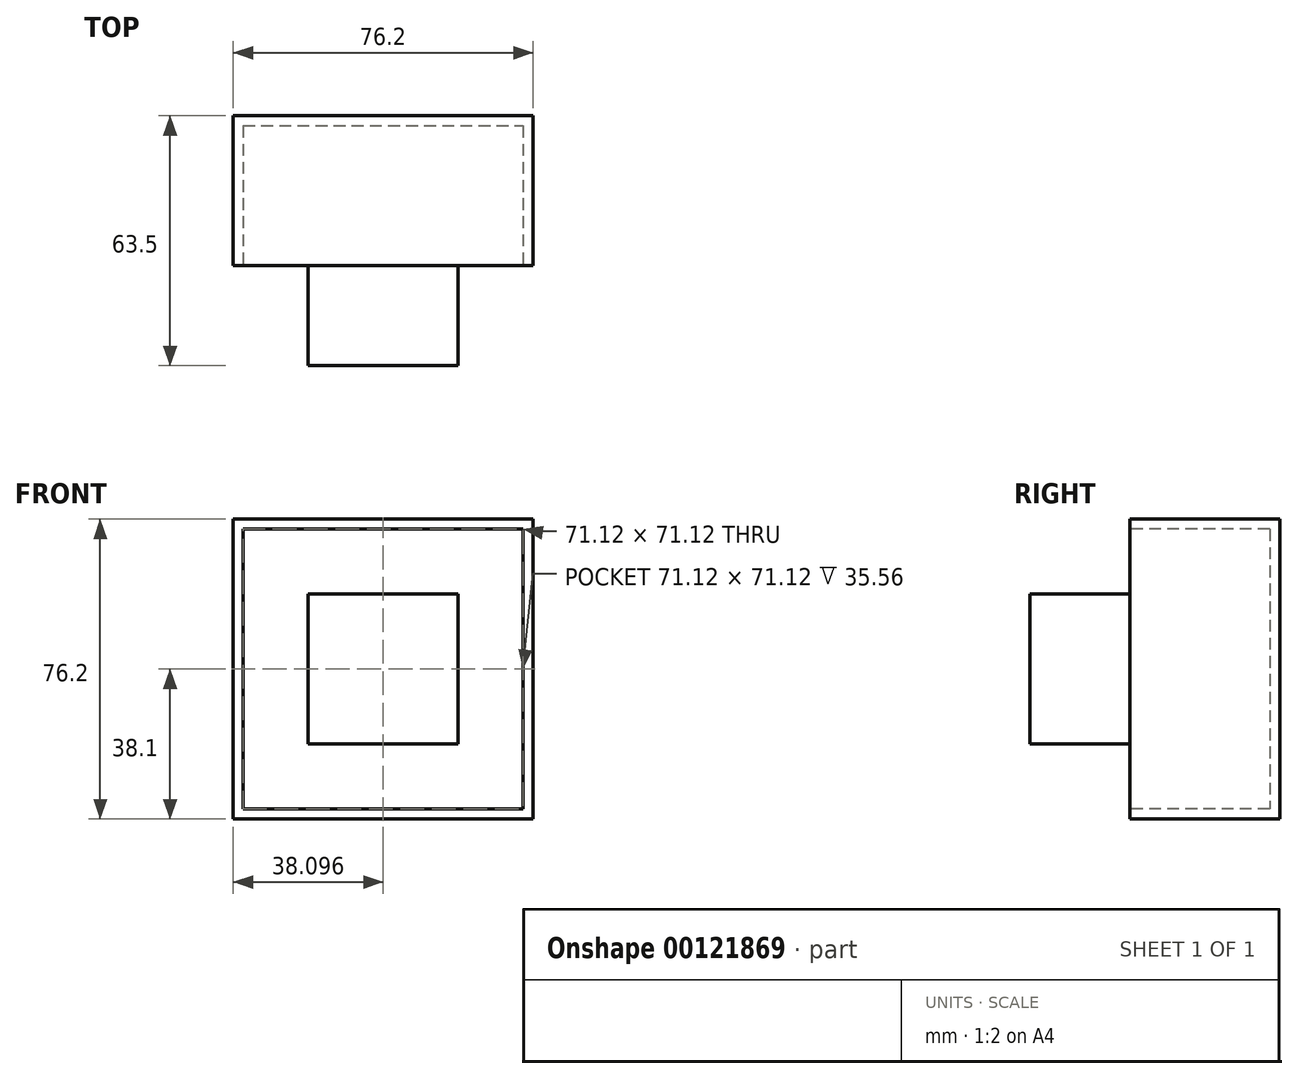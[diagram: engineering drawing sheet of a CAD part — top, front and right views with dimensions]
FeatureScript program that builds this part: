
annotation { "Feature Type Name" : "Feature", "Feature Type Description" : "" }
export const myFeature = defineFeature(function(context is Context, id is Id, definition is map)
    precondition{}
    {
        {
            var Q0;
            Q0=qCreatedBy(makeId("Top.planeOp"),FACE);
            var sketch = newSketch(context, id + "F0", { "sketchPlane" : qUnion([Q0])});
            skLineSegment(sketch, "E0.bottom", {"start": v(-38.65, 15.85) * mm, "end": v(37.55, 15.85) * mm});
            skLineSegment(sketch, "E0.top", {"start": v(-38.65, -22.25) * mm, "end": v(37.55, -22.25) * mm});
            skLineSegment(sketch, "E0.left", {"start": v(-38.65, 15.85) * mm, "end": v(-38.65, -22.25) * mm});
            skLineSegment(sketch, "E0.right", {"start": v(37.55, 15.85) * mm, "end": v(37.55, -22.25) * mm});
            skSolve(sketch);
        }
        {
            var Q0;
            Q0 = qSketchRegion(id + "F0", true);
            extrude(context, id + "F1", {"entities" : qUnion([Q0]), "depth" : 76.2 * mm});
        }
        {
            var Q0;
            Q0=makeQuery(id+"F1.opExtrude","SWEPT_FACE",FACE,{"disambiguationData":[OSD([sQuery(id+"F0.wireOp",EDGE,"E0.top")])]});
            var sketch = newSketch(context, id + "F2", { "sketchPlane" : qUnion([Q0])});
            skLineSegment(sketch, "E1.bottom", {"start": v(-19.6, 57.15) * mm, "end": v(18.5, 57.15) * mm});
            skLineSegment(sketch, "E1.top", {"start": v(-19.6, 19.05) * mm, "end": v(18.5, 19.05) * mm});
            skLineSegment(sketch, "E1.left", {"start": v(-19.6, 57.15) * mm, "end": v(-19.6, 19.05) * mm});
            skLineSegment(sketch, "E1.right", {"start": v(18.5, 57.15) * mm, "end": v(18.5, 19.05) * mm});
            skSolve(sketch);
        }
        {
            var Q0;
            Q0=makeQuery(id+"F1.opExtrude","SWEPT_FACE",FACE,{"disambiguationData":[OSD([sQuery(id+"F0.wireOp",EDGE,"E0.top")])]});
            shell(context, id + "F3", {"entities" : qUnion([Q0]), "thickness" : 2.54 * mm});
        }
        {
            var Q0;
            Q0=makeQuery(id+"F2.imprint","IMPRINT",FACE,{"disambiguationData":[TD([[makeQuery(id+"F2.imprint","IMPRINT",EDGE,{"derivedFrom":sQuery(id+"F2.wireOp",EDGE,"E1.bottom")}),-1.0]])]});
            extrude(context, id + "F4", {"entities" : qUnion([Q0]), "depth" : 25.4 * mm});
        }
    });
